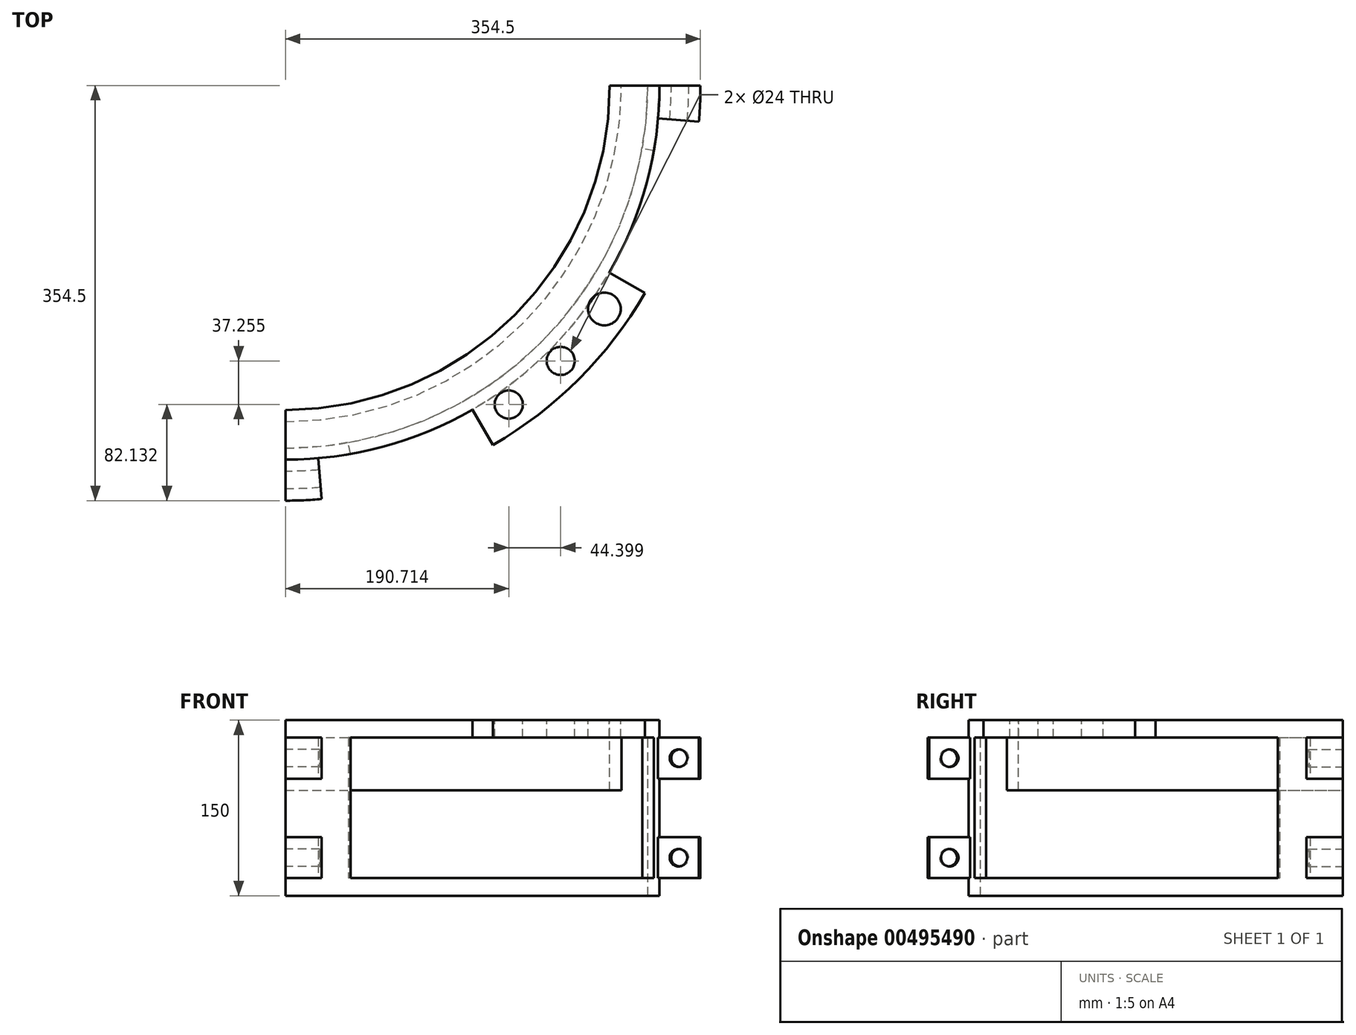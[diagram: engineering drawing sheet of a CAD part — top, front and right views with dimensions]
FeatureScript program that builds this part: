
annotation { "Feature Type Name" : "Feature", "Feature Type Description" : "" }
export const myFeature = defineFeature(function(context is Context, id is Id, definition is map)
    precondition{}
    {
        {
            var Q0;
            Q0=qCreatedBy(makeId("Front.planeOp"),FACE);
            var sketch = newSketch(context, id + "F0", { "sketchPlane" : qUnion([Q0])});
            skLineSegment(sketch, "E0", {"start": v(0, 74.16) * mm, "end": v(0, -86.7) * mm});
            skLineSegment(sketch, "E1", {"start": v(-10, -75.84) * mm, "end": v(-10, 59.16) * mm});
            skLineSegment(sketch, "E2", {"start": v(-10, 59.16) * mm, "end": v(-32.5, 59.16) * mm});
            skLineSegment(sketch, "E3", {"start": v(-32.5, 59.16) * mm, "end": v(-32.5, 14.16) * mm});
            skLineSegment(sketch, "E4", {"start": v(-32.5, 14.16) * mm, "end": v(-42.5, 14.16) * mm});
            skLineSegment(sketch, "E5", {"start": v(-42.5, 14.16) * mm, "end": v(-42.5, 74.16) * mm});
            skLineSegment(sketch, "E6", {"start": v(-42.5, 74.16) * mm, "end": v(0, 74.16) * mm});
            skLineSegment(sketch, "E7", {"start": v(-319.5, 365.07) * mm, "end": v(-319.5, -375.83) * mm});
            skLineSegment(sketch, "E8", {"start": v(0, -75.84) * mm, "end": v(0, -86.7) * mm});
            skLineSegment(sketch, "E9", {"start": v(0, -75.84) * mm, "end": v(-10, -75.84) * mm});
            skSolve(sketch);
        }
        {
            var Q0;
            Q0=makeQuery(id+"F0.imprint","IMPRINT",FACE,{"disambiguationData":[TD([[makeQuery(id+"F0.imprint","IMPRINT",EDGE,{"derivedFrom":sQuery(id+"F0.wireOp",EDGE,"E0")}),-1.0]])]});
            var Q1;
            Q1=sQuery(id+"F0.wireOp",EDGE,"E7");
            revolve(context, id + "F1", {"entities" : qUnion([Q0]), "axis" : qUnion([Q1]), "revolveType" : RevolveType.ONE_DIRECTION, "angle" : 90 * degree});
        }
        {
            var Q0;
            Q0=makeQuery(id+"F1.opRevolve","CAP_FACE",FACE,{"disambiguationData":[OSD([sQuery(id+"F0.wireOp",EDGE,"E0"),sQuery(id+"F0.wireOp",EDGE,"y736AHZ5-NndI-1HCs-AYic-F7srbCbLnXGM"),sQuery(id+"F0.wireOp",EDGE,"aa7eJtI8-twBU-IfdB-iQKM-DBjtKeOemjLS"),sQuery(id+"F0.wireOp",EDGE,"9Gu4vQGe-gWwg-p7A0-avW0-QwNsrsUvMnfG"),sQuery(id+"F0.wireOp",EDGE,"E1"),sQuery(id+"F0.wireOp",EDGE,"E2"),sQuery(id+"F0.wireOp",EDGE,"E3"),sQuery(id+"F0.wireOp",EDGE,"E4"),sQuery(id+"F0.wireOp",EDGE,"E5"),sQuery(id+"F0.wireOp",EDGE,"E6")])],"isStart":false});
            var sketch = newSketch(context, id + "F2", { "sketchPlane" : qUnion([Q0])});
            skLineSegment(sketch, "E10.bottom", {"start": v(319.5, 59.16) * mm, "end": v(354.5, 59.16) * mm});
            skLineSegment(sketch, "E10.top", {"start": v(319.5, 24.16) * mm, "end": v(354.5, 24.16) * mm});
            skLineSegment(sketch, "E10.left", {"start": v(319.5, 59.16) * mm, "end": v(319.5, 24.16) * mm});
            skLineSegment(sketch, "E10.right", {"start": v(354.5, 59.16) * mm, "end": v(354.5, 24.16) * mm});
            skCircle(sketch, "E11", {"center": v(337, 41.66) * mm, "radius": 7.5 * mm});
            skPoint(sketch, "E11.centerSnap0", {"position": v(337, 59.16) * mm});
            skPoint(sketch, "E11.centerSnap1", {"position": v(319.5, 41.66) * mm});
            skLineSegment(sketch, "E12.bottom", {"start": v(319.5, -25.84) * mm, "end": v(354.5, -25.84) * mm});
            skLineSegment(sketch, "E12.top", {"start": v(319.5, -60.84) * mm, "end": v(354.5, -60.84) * mm});
            skLineSegment(sketch, "E12.left", {"start": v(319.5, -25.84) * mm, "end": v(319.5, -60.84) * mm});
            skLineSegment(sketch, "E12.right", {"start": v(354.5, -25.84) * mm, "end": v(354.5, -60.84) * mm});
            skCircle(sketch, "E13", {"center": v(337, -43.34) * mm, "radius": 7.5 * mm});
            skPoint(sketch, "E13.centerSnap0", {"position": v(337, -25.84) * mm});
            skPoint(sketch, "E13.centerSnap1", {"position": v(319.5, -43.34) * mm});
            skLineSegment(sketch, "E14", {"start": v(0, 230.54) * mm, "end": v(0, -215.96) * mm});
            skSolve(sketch);
        }
        {
            var Q0;
            Q0=qSketchRegion(id+"F2",true);
            var Q1;
            Q1=sQuery(id+"F2.wireOp",EDGE,"E14");
            revolve(context, id + "F3", {"operationType" : NewBodyOperationType.ADD, "entities" : qUnion([Q0]), "axis" : qUnion([Q1]), "revolveType" : RevolveType.ONE_DIRECTION, "oppositeDirection" : true, "angle" : 5 * degree});
        }
        {
            var Q0;
            Q0=qSketchRegion(id+"F2",true);
            var Q1;
            Q1=makeQuery(id+"F1.opRevolve","SWEPT_FACE",FACE,{"disambiguationData":[OSD([sQuery(id+"F0.wireOp",EDGE,"E5")])]});
            revolve(context, id + "F4", {"operationType" : NewBodyOperationType.ADD, "entities" : qUnion([Q0]), "axis" : qUnion([Q1]), "revolveType" : RevolveType.TWO_DIRECTIONS, "angle" : 275 * degree, "angleBack" : 270 * degree});
        }
        {
            var Q0;
            Q0=qCreatedBy(makeId("Front.planeOp"),FACE);
            var sketch = newSketch(context, id + "F5", { "sketchPlane" : qUnion([Q0])});
            skLineSegment(sketch, "E15.bottom", {"start": v(0, 59.16) * mm, "end": v(-10, 59.16) * mm});
            skLineSegment(sketch, "E15.top", {"start": v(0, -60.84) * mm, "end": v(-10, -60.84) * mm});
            skLineSegment(sketch, "E15.left", {"start": v(0, 59.16) * mm, "end": v(0, -60.84) * mm});
            skLineSegment(sketch, "E15.right", {"start": v(-10, 59.16) * mm, "end": v(-10, -60.84) * mm});
            skLineSegment(sketch, "E16", {"start": v(-319.5, 127.34) * mm, "end": v(-319.5, -187.15) * mm});
            skSolve(sketch);
        }
        {
            var Q0;
            Q0=qSketchRegion(id+"F5",true);
            var Q1;
            Q1=sQuery(id+"F5.wireOp",EDGE,"E16");
            revolve(context, id + "F6", {"operationType" : NewBodyOperationType.REMOVE, "entities" : qUnion([Q0]), "axis" : qUnion([Q1]), "revolveType" : RevolveType.TWO_DIRECTIONS, "oppositeDirection" : true, "angle" : 350 * degree, "angleBack" : 280 * degree});
        }
        {
            var Q0;
            Q0=qCreatedBy(makeId("Front.planeOp"),FACE);
            var sketch = newSketch(context, id + "F7", { "sketchPlane" : qUnion([Q0])});
            skLineSegment(sketch, "E17", {"start": v(0, 74.16) * mm, "end": v(35, 74.16) * mm});
            skLineSegment(sketch, "E18", {"start": v(35, 74.16) * mm, "end": v(35, 59.16) * mm});
            skLineSegment(sketch, "E19", {"start": v(35, 59.16) * mm, "end": v(0, 59.16) * mm});
            skLineSegment(sketch, "E20", {"start": v(0, 59.16) * mm, "end": v(0, 74.16) * mm});
            skLineSegment(sketch, "E21", {"start": v(-319.5, 145.83) * mm, "end": v(-319.5, -234.64) * mm});
            skSolve(sketch);
        }
        {
            var Q0;
            Q0=makeQuery(id+"F7.imprint","IMPRINT",FACE,{"disambiguationData":[TD([[makeQuery(id+"F7.imprint","IMPRINT",EDGE,{"derivedFrom":sQuery(id+"F7.wireOp",EDGE,"E17")}),-1.0]])]});
            var Q1;
            Q1=sQuery(id+"F7.wireOp",EDGE,"E21");
            revolve(context, id + "F8", {"operationType" : NewBodyOperationType.ADD, "entities" : qUnion([Q0]), "axis" : qUnion([Q1]), "revolveType" : RevolveType.TWO_DIRECTIONS, "angle" : 60 * degree, "angleBack" : 30 * degree});
        }
        {
            var Q0;
            Q0=makeQuery(id+"F8.boolean.opBoolean","MERGE",FACE,{"derivedFrom":[makeQuery(id+"F1.opRevolve","SWEPT_FACE",FACE,{"disambiguationData":[OSD([sQuery(id+"F0.wireOp",EDGE,"E6")])]}),makeQuery(id+"F8.opRevolve","SWEPT_FACE",FACE,{"disambiguationData":[OSD([sQuery(id+"F7.wireOp",EDGE,"E17")])]})]});
            var sketch = newSketch(context, id + "F9", { "sketchPlane" : qUnion([Q0])});
            skCircle(sketch, "E22", {"center": v(-128.79, -272.37) * mm, "radius": 12 * mm});
            skCircle(sketch, "E23", {"center": v(-84.39, -235.11) * mm, "radius": 12 * mm});
            skCircle(sketch, "E24", {"center": v(-47.13, -190.71) * mm, "radius": 14 * mm});
            skCircle(sketch, "E25", {"center": v(-319.5, 0) * mm, "radius": 277 * mm});
            skCircle(sketch, "E26", {"center": v(-319.5, 0) * mm, "radius": 332.5 * mm});
            skLineSegment(sketch, "E27", {"start": v(-319.5, 0) * mm, "end": v(-84.39, -235.11) * mm});
            skLineSegment(sketch, "E28", {"start": v(-319.5, 0) * mm, "end": v(0, 0) * mm});
            skLineSegment(sketch, "E29", {"start": v(-319.5, 0) * mm, "end": v(-47.13, -190.71) * mm});
            skLineSegment(sketch, "E30", {"start": v(-319.5, 0) * mm, "end": v(-128.79, -272.37) * mm});
            skSolve(sketch);
        }
        {
            var Q0;
            {var subQ0=sQuery(id+"F9.wireOp",EDGE,"E30");var subQ1=sQuery(id+"F9.wireOp",EDGE,"E22");var subQ2=makeQuery(id+"F9.imprint","INTERSECT",VERTEX,{"derivedFrom":[subQ1,subQ0]});Q0=makeQuery(id+"F9.imprint","IMPRINT",FACE,{"disambiguationData":[TD([[makeQuery(id+"F9.imprint","IMPRINT",EDGE,{"disambiguationData":[TD([[subQ2,1.0]])],"derivedFrom":subQ1}),1.0]])]});}
            var Q1;
            {var subQ0=sQuery(id+"F9.wireOp",EDGE,"E26");var subQ1=sQuery(id+"F9.wireOp",EDGE,"E22");var subQ2=makeQuery(id+"F9.imprint","INTERSECT",VERTEX,{"disambiguationData":[OD(0.0)],"derivedFrom":[subQ1,subQ0]});Q1=makeQuery(id+"F9.imprint","IMPRINT",FACE,{"disambiguationData":[TD([[makeQuery(id+"F9.imprint","IMPRINT",EDGE,{"disambiguationData":[TD([[subQ2,1.0]])],"derivedFrom":subQ1}),1.0]])]});}
            var Q2;
            {var subQ0=sQuery(id+"F9.wireOp",EDGE,"E30");var subQ1=sQuery(id+"F9.wireOp",EDGE,"E22");var subQ2=makeQuery(id+"F9.imprint","INTERSECT",VERTEX,{"derivedFrom":[subQ1,subQ0]});Q2=makeQuery(id+"F9.imprint","IMPRINT",FACE,{"disambiguationData":[TD([[makeQuery(id+"F9.imprint","IMPRINT",EDGE,{"disambiguationData":[TD([[subQ2,-1.0]])],"derivedFrom":subQ1}),1.0]])]});}
            var Q3;
            {var subQ0=sQuery(id+"F9.wireOp",EDGE,"E27");var subQ1=sQuery(id+"F9.wireOp",EDGE,"E23");var subQ2=makeQuery(id+"F9.imprint","INTERSECT",VERTEX,{"derivedFrom":[subQ1,subQ0]});Q3=makeQuery(id+"F9.imprint","IMPRINT",FACE,{"disambiguationData":[TD([[makeQuery(id+"F9.imprint","IMPRINT",EDGE,{"disambiguationData":[TD([[subQ2,-1.0]])],"derivedFrom":subQ1}),1.0]])]});}
            var Q4;
            {var subQ0=sQuery(id+"F9.wireOp",EDGE,"E26");var subQ1=sQuery(id+"F9.wireOp",EDGE,"E23");var subQ2=makeQuery(id+"F9.imprint","INTERSECT",VERTEX,{"disambiguationData":[OD(0.0)],"derivedFrom":[subQ1,subQ0]});Q4=makeQuery(id+"F9.imprint","IMPRINT",FACE,{"disambiguationData":[TD([[makeQuery(id+"F9.imprint","IMPRINT",EDGE,{"disambiguationData":[TD([[subQ2,1.0]])],"derivedFrom":subQ1}),1.0]])]});}
            var Q5;
            {var subQ0=sQuery(id+"F9.wireOp",EDGE,"E27");var subQ1=sQuery(id+"F9.wireOp",EDGE,"E23");var subQ2=makeQuery(id+"F9.imprint","INTERSECT",VERTEX,{"derivedFrom":[subQ1,subQ0]});Q5=makeQuery(id+"F9.imprint","IMPRINT",FACE,{"disambiguationData":[TD([[makeQuery(id+"F9.imprint","IMPRINT",EDGE,{"disambiguationData":[TD([[subQ2,1.0]])],"derivedFrom":subQ1}),1.0]])]});}
            var Q6;
            {var subQ0=sQuery(id+"F9.wireOp",EDGE,"E26");var subQ1=sQuery(id+"F9.wireOp",EDGE,"E24");var subQ2=makeQuery(id+"F9.imprint","INTERSECT",VERTEX,{"disambiguationData":[OD(0.0)],"derivedFrom":[subQ1,subQ0]});Q6=makeQuery(id+"F9.imprint","IMPRINT",FACE,{"disambiguationData":[TD([[makeQuery(id+"F9.imprint","IMPRINT",EDGE,{"disambiguationData":[TD([[subQ2,1.0]])],"derivedFrom":subQ1}),1.0]])]});}
            var Q7;
            {var subQ0=sQuery(id+"F9.wireOp",EDGE,"E29");var subQ1=sQuery(id+"F9.wireOp",EDGE,"E24");var subQ2=makeQuery(id+"F9.imprint","INTERSECT",VERTEX,{"derivedFrom":[subQ1,subQ0]});Q7=makeQuery(id+"F9.imprint","IMPRINT",FACE,{"disambiguationData":[TD([[makeQuery(id+"F9.imprint","IMPRINT",EDGE,{"disambiguationData":[TD([[subQ2,-1.0]])],"derivedFrom":subQ1}),1.0]])]});}
            var Q8;
            {var subQ0=sQuery(id+"F9.wireOp",EDGE,"E29");var subQ1=sQuery(id+"F9.wireOp",EDGE,"E24");var subQ2=makeQuery(id+"F9.imprint","INTERSECT",VERTEX,{"derivedFrom":[subQ1,subQ0]});Q8=makeQuery(id+"F9.imprint","IMPRINT",FACE,{"disambiguationData":[TD([[makeQuery(id+"F9.imprint","IMPRINT",EDGE,{"disambiguationData":[TD([[subQ2,1.0]])],"derivedFrom":subQ1}),1.0]])]});}
            extrude(context, id + "F10", {"entities" : qUnion([Q0, Q1, Q2, Q3, Q4, Q5, Q6, Q7, Q8]), "operationType" : NewBodyOperationType.REMOVE, "oppositeDirection" : true, "depth" : 15 * mm});
        }
    });
